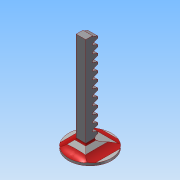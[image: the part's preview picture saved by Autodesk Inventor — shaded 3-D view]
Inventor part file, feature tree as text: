
AUTODESK INVENTOR PART (.ipt)
format: ipt  version: 2015 (Build 190159000, 159)  size: 258,048 bytes
history: native  units: mm
features: other x3, fillet x1
ambient origin geometry x8: Origin, YZ Plane, XZ Plane, XY Plane, X Axis, Y Axis, Z Axis, Center Point
bodies: Volumenkörper1 (feature_tree)
feature tree (4):
  other  "Membran_Platte_V4_1.iam"
  other  "Membran_Platte_V4.ipt:1"
  other  "Zahnstange.ipt:1"
  fillet  "Rundung2"  Radius=10.0mm
